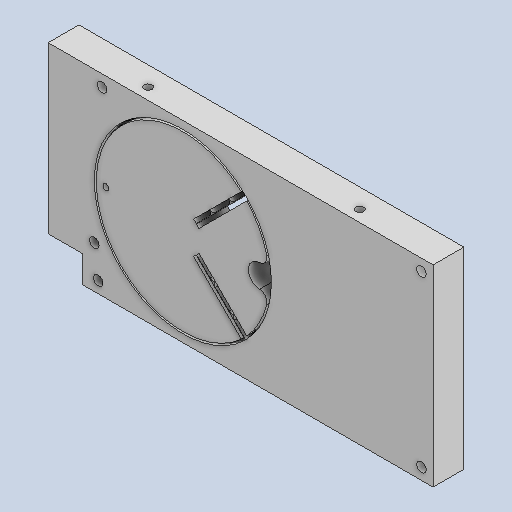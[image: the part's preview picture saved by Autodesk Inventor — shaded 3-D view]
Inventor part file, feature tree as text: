
AUTODESK INVENTOR PART (.ipt)
format: ipt  version: 2023 (Build 270158000, 158)  size: 308,736 bytes
history: native  units: mm
features: extrude x7, sketch x7, reference x6, other x5, fillet x1
ambient origin geometry x8: Origin, YZ Plane, XZ Plane, XY Plane, X Axis, Y Axis, Z Axis, Center Point
bodies: Solid1 (feature_tree)
feature tree (26):
  extrude  "Extrusion1"  Depth=100.0mm
  extrude  "Extrusion4"  Depth=5.0mm
  fillet  "Fillet2"  Radius=5.0mm
  extrude  "Extrusion5"  Depth=5.0mm
  extrude  "Extrusion6"  Depth=15.0mm
  extrude  "Extrusion7"  Depth=3.5mm
  extrude  "Extrusion8"  Depth=3.5mm
  extrude  "Extrusion9"  Depth=10.0mm TaperAngle=0.0deg
  sketch  "Sketch1"  dims[d0=50.0mm d1=100.0mm]
  sketch  "Sketch4"  dims[d2=5.0mm d3=5.0mm d4=5.0mm]
  sketch  "Sketch5"  dims[d5=5.0mm d6=5.0mm]
  sketch  "Sketch6"  dims[d7=15.0mm d8=15.0mm]
  reference  "Reference4"
  reference  "Reference5"
  sketch  "Sketch7"  dims[d9=5.0mm d10=3.5mm]
  reference  "Reference6"
  reference  "Reference7"
  reference  "Reference9"
  reference  "Reference10"
  sketch  "Sketch8"  dims[d11=3.5mm d12=3.5mm]
  sketch  "Sketch9"  dims[d13=3.5mm d14=8.0mm d15=0.0mm d22=15.0mm d23=40.0mm d24=20.0mm d25=45.0mm d26=1.6mm d27=6.0mm d28=45.0deg d29=45.0deg d30=46.0mm d31=25.0mm d32=25.0mm d33=25.0mm d34=10.0mm d35=1.0mm d36=1.0mm d37=0.1mm d38=0.05mm d39=0.1mm d40=0.05mm d41=1.0mm d42=1.0mm d43=8.0mm d44=0.0mm d46=2.0mm d47=15.0mm d48=1.5mm d49=9.0mm d50=0.0mm d51=7.0mm d52=1.6mm d53=1.6mm d54=8.0mm d55=0.0mm d56=2.5mm d57=2.5mm d58=2.5mm d59=2.5mm d60=2.5mm d61=8.0mm d62=0.0mm d63=2.5mm d64=3.0mm d65=4.0mm d66=8.0mm d67=0.0mm d68=2.05mm d69=2.05mm d70=2.05mm d71=2.05mm d72=8.0mm d73=0.0mm d74=23.0mm d75=23.0mm d76=55.0mm d77=23.0mm d78=55.0mm d79=5.0mm d80=2.0mm d81=5.0mm d82=2.0mm d83=5.0mm d84=2.0mm d85=5.0mm d86=2.0mm]
  other  "<userpath>\ClawdDrive\Objet3D\IminaProbe\V3Roue\RoueV3.iam"
  other  "RoueV3.iam"
  other  "CapacitiveSensor:1"
  other  "RoueV3PartB:1"
  other  "RoueV3PartC:1"
